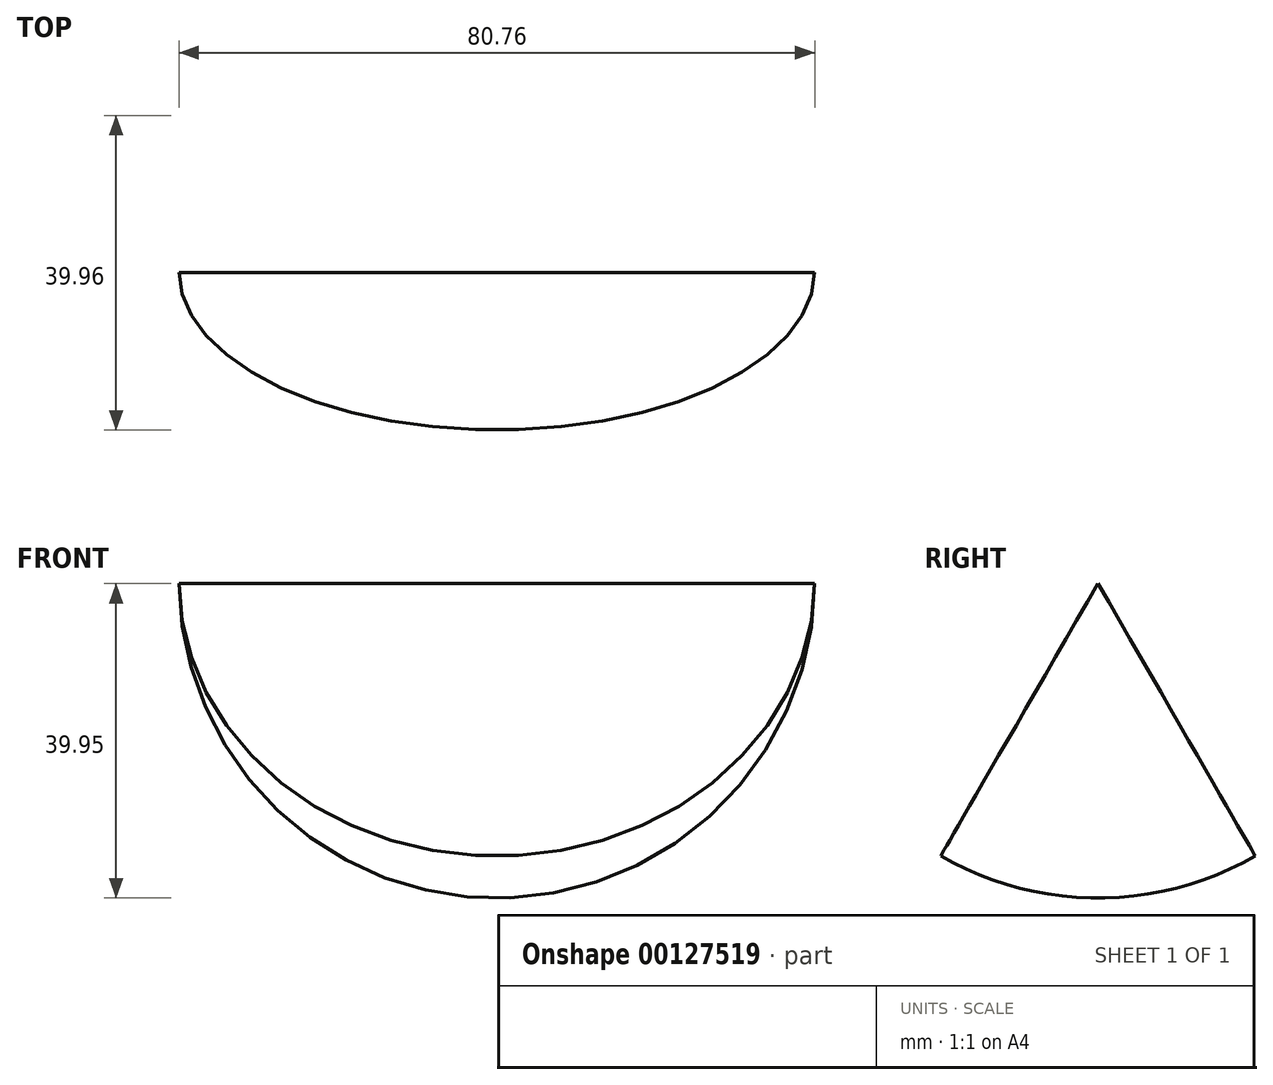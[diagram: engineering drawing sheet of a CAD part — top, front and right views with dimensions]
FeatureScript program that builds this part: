
annotation { "Feature Type Name" : "Feature", "Feature Type Description" : "" }
export const myFeature = defineFeature(function(context is Context, id is Id, definition is map)
    precondition{}
    {
        {
            var Q0;
            Q0=qCreatedBy(makeId("Front.planeOp"),FACE);
            var sketch = newSketch(context, id + "F0", { "sketchPlane" : qUnion([Q0])});
            skArc(sketch, "E0", {"start": v(-41.72, 0) * mm, "mid": v(-1.34, -39.95) * mm, "end": v(39.04, 0) * mm});
            skLineSegment(sketch, "E1", {"start": v(-41.72, 0) * mm, "end": v(39.04, 0) * mm});
            skSolve(sketch);
        }
        {
            var Q0;
            Q0 = qSketchRegion(id + "F0", true);
            var Q1;
            Q1=sQuery(id+"F0.wireOp",EDGE,"E1");
            revolve(context, id + "F1", {"entities" : qUnion([Q0]), "axis" : qUnion([Q1]), "revolveType" : RevolveType.TWO_DIRECTIONS, "angle" : 30 * degree, "angleBack" : 330 * degree});
        }
    });
